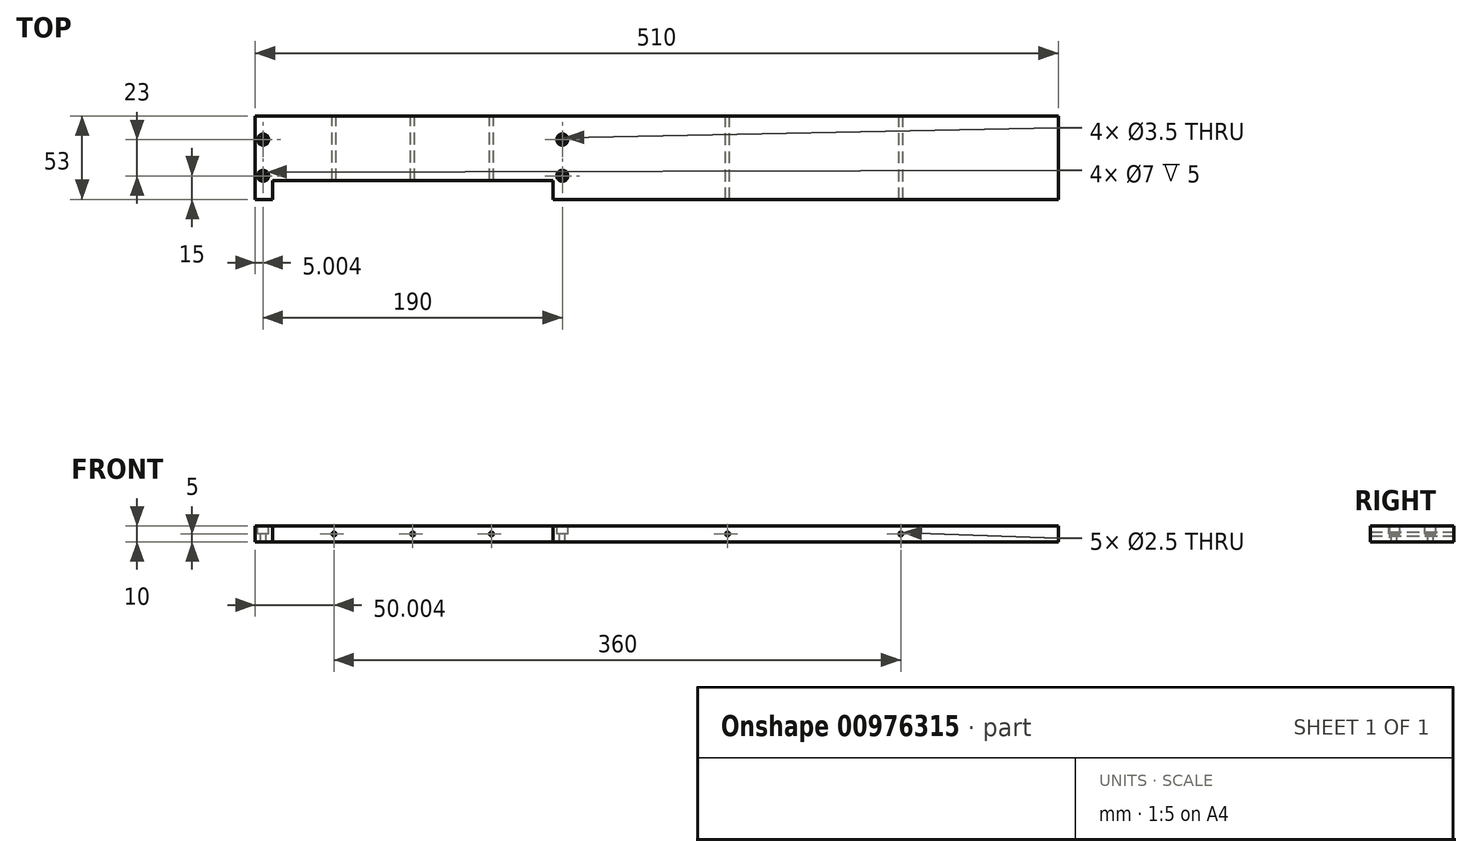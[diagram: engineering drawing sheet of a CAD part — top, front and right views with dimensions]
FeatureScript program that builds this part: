
annotation { "Feature Type Name" : "Feature", "Feature Type Description" : "" }
export const myFeature = defineFeature(function(context is Context, id is Id, definition is map)
    precondition{}
    {
        {
            var Q0;
            Q0=qCreatedBy(makeId("Top.planeOp"),FACE);
            var sketch = newSketch(context, id + "F0", { "sketchPlane" : qUnion([Q0])});
            skLineSegment(sketch, "E0.bottom", {"start": v(-229.19, -6.8) * mm, "end": v(280.81, -6.8) * mm});
            skLineSegment(sketch, "E0.top", {"start": v(-229.19, -59.8) * mm, "end": v(280.81, -59.8) * mm});
            skLineSegment(sketch, "E0.left", {"start": v(-229.19, -6.8) * mm, "end": v(-229.19, -59.8) * mm});
            skLineSegment(sketch, "E0.right", {"start": v(280.81, -6.8) * mm, "end": v(280.81, -59.8) * mm});
            skLineSegment(sketch, "E1", {"start": v(-218.19, -59.8) * mm, "end": v(-218.19, -47.8) * mm});
            skLineSegment(sketch, "E2", {"start": v(-218.19, -47.8) * mm, "end": v(-40.19, -47.8) * mm});
            skLineSegment(sketch, "E3", {"start": v(-40.19, -47.8) * mm, "end": v(-40.19, -59.8) * mm});
            skLineSegment(sketch, "E4", {"start": v(-219.19, -59.8) * mm, "end": v(-219.19, -6.8) * mm});
            skLineSegment(sketch, "E5", {"start": v(-39.19, -6.8) * mm, "end": v(-39.19, -59.8) * mm});
            skLineSegment(sketch, "E6", {"start": v(-29.19, -59.8) * mm, "end": v(-29.19, -6.8) * mm});
            skSolve(sketch);
        }
        {
            var Q0;
            Q0=makeQuery(id+"F0.imprint","IMPRINT",FACE,{"disambiguationData":[TD([[makeQuery(id+"F0.imprint","IMPRINT",EDGE,{"derivedFrom":sQuery(id+"F0.wireOp",EDGE,"E0.bottom")}),-1.0]])]});
            var Q1;
            {var subQ0=sQuery(id+"F0.wireOp",EDGE,"E1");Q1=makeQuery(id+"F0.imprint","IMPRINT",FACE,{"disambiguationData":[TD([[makeQuery(id+"F0.imprint","IMPRINT",EDGE,{"derivedFrom":subQ0}),1.0]])]});}
            extrude(context, id + "F1", {"entities" : qUnion([Q0, Q1]), "depth" : 10 * mm, "offsetDistance" : 25 * mm});
        }
        {
            var Q0;
            Q0=makeQuery(id+"F1.opExtrude","CAP_FACE",FACE,{"disambiguationData":[OSD([sQuery(id+"F0.wireOp",EDGE,"E0.bottom"),sQuery(id+"F0.wireOp",EDGE,"E0.top"),sQuery(id+"F0.wireOp",EDGE,"E0.left"),sQuery(id+"F0.wireOp",EDGE,"E0.right"),sQuery(id+"F0.wireOp",EDGE,"E1"),sQuery(id+"F0.wireOp",EDGE,"E2"),sQuery(id+"F0.wireOp",EDGE,"E3")])],"isStart":false});
            var sketch = newSketch(context, id + "F2", { "sketchPlane" : qUnion([Q0])});
            skCircle(sketch, "E7", {"center": v(-224.19, -21.8) * mm, "radius": 2.5 * mm});
            skCircle(sketch, "E8", {"center": v(-224.19, -44.8) * mm, "radius": 2.5 * mm});
            skCircle(sketch, "E9", {"center": v(-34.19, -21.8) * mm, "radius": 2.5 * mm});
            skCircle(sketch, "E10", {"center": v(-34.19, -44.8) * mm, "radius": 2.5 * mm});
            skSolve(sketch);
        }
        {
            var Q0;
            Q0=sQuery(id+"F2.wireOp",VERTEX,"E7.center");
            var Q1;
            Q1=sQuery(id+"F2.wireOp",VERTEX,"E8.center");
            var Q2;
            Q2=sQuery(id+"F2.wireOp",VERTEX,"E9.center");
            var Q3;
            Q3=sQuery(id+"F2.wireOp",VERTEX,"E10.center");
            var Q4;
            Q4=makeQuery(id+"F1.opExtrude","SWEPT_BODY",BODY,{"disambiguationData":[OSD([sQuery(id+"F0.wireOp",EDGE,"E0.bottom"),sQuery(id+"F0.wireOp",EDGE,"E0.top"),sQuery(id+"F0.wireOp",EDGE,"E0.left"),sQuery(id+"F0.wireOp",EDGE,"E0.right"),sQuery(id+"F0.wireOp",EDGE,"E1"),sQuery(id+"F0.wireOp",EDGE,"E2"),sQuery(id+"F0.wireOp",EDGE,"E3")])]});
            hole(context, id + "F3", {"style" : HoleStyle.C_BORE, "endStyle" : HoleEndStyle.THROUGH, "holeDiameter" : 3.5 * mm, "cBoreDiameter" : 7 * mm, "cBoreDepth" : 5 * mm, "majorDiameter" : 4 * mm, "isTappedThrough" : true, "tappedDepth" : 19.25 * mm, "tapClearance" : 3, "locations" : qUnion([Q0, Q1, Q2, Q3]), "scope" : qUnion([Q4])});
        }
        {
            var Q0;
            Q0=makeQuery(id+"F1.opExtrude","SWEPT_FACE",FACE,{"disambiguationData":[OSD([sQuery(id+"F0.wireOp",EDGE,"E0.bottom")])]});
            var sketch = newSketch(context, id + "F4", { "sketchPlane" : qUnion([Q0])});
            skLineSegment(sketch, "E11", {"start": v(29.19, 10) * mm, "end": v(29.19, 0) * mm});
            skCircle(sketch, "E12", {"center": v(79.19, 5) * mm, "radius": 1.25 * mm});
            skCircle(sketch, "E13", {"center": v(129.19, 5) * mm, "radius": 1.25 * mm});
            skCircle(sketch, "E14", {"center": v(179.19, 5) * mm, "radius": 1.25 * mm});
            skCircle(sketch, "E15", {"center": v(-70.81, 5) * mm, "radius": 1.25 * mm});
            skCircle(sketch, "E16", {"center": v(-180.81, 5) * mm, "radius": 1.25 * mm});
            skSolve(sketch);
        }
        {
            var Q0;
            Q0=makeQuery(id+"F4.imprint","IMPRINT",FACE,{"disambiguationData":[TD([[makeQuery(id+"F4.imprint","IMPRINT",EDGE,{"derivedFrom":sQuery(id+"F4.wireOp",EDGE,"E16")}),1.0]])]});
            var Q1;
            Q1=makeQuery(id+"F4.imprint","IMPRINT",FACE,{"disambiguationData":[TD([[makeQuery(id+"F4.imprint","IMPRINT",EDGE,{"derivedFrom":sQuery(id+"F4.wireOp",EDGE,"E15")}),1.0]])]});
            var Q2;
            Q2=makeQuery(id+"F4.imprint","IMPRINT",FACE,{"disambiguationData":[TD([[makeQuery(id+"F4.imprint","IMPRINT",EDGE,{"derivedFrom":sQuery(id+"F4.wireOp",EDGE,"E12")}),1.0]])]});
            var Q3;
            Q3=makeQuery(id+"F4.imprint","IMPRINT",FACE,{"disambiguationData":[TD([[makeQuery(id+"F4.imprint","IMPRINT",EDGE,{"derivedFrom":sQuery(id+"F4.wireOp",EDGE,"E13")}),1.0]])]});
            var Q4;
            Q4=makeQuery(id+"F4.imprint","IMPRINT",FACE,{"disambiguationData":[TD([[makeQuery(id+"F4.imprint","IMPRINT",EDGE,{"derivedFrom":sQuery(id+"F4.wireOp",EDGE,"E14")}),1.0]])]});
            extrude(context, id + "F5", {"entities" : qUnion([Q0, Q1, Q2, Q3, Q4]), "operationType" : NewBodyOperationType.REMOVE, "endBound" : BoundingType.UP_TO_NEXT, "oppositeDirection" : true, "depth" : 25 * mm, "offsetDistance" : 25 * mm});
        }
    });
